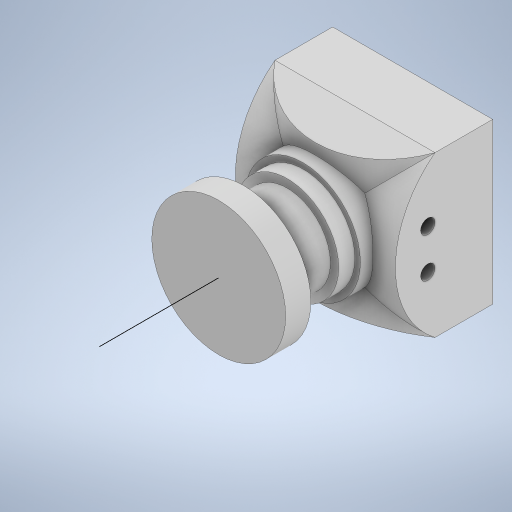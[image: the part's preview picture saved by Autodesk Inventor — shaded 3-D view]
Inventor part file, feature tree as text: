
AUTODESK INVENTOR PART (.ipt)
format: ipt  version: 2023 (Build 270158000, 158)  size: 365,568 bytes
history: native  units: in
note: dims shown in document units (in); Inventor stores cm internally (conversion verified against a paired STEP export)
features: sketch x12, extrude x9, projected_geometry x7, plane x2
ambient origin geometry x8: Origin, YZ Plane, XZ Plane, XY Plane, X Axis, Y Axis, Z Axis, Center Point
bodies: Solid1 (feature_tree)
feature tree (30):
  extrude  "Extrusion1"  Depth=0.874in
  extrude  "Extrusion2"  Depth=0.315in
  sketch  "Sketch3"  dims[d5=0.2854in d6=0.0in d9=0.2165in]
  extrude  "Extrusion4"  Depth=0.2165in
  extrude  "Extrusion5"  Depth=0.0886in
  extrude  "Extrusion6"  Depth=0.374in
  extrude  "Extrusion8"  Depth=0.0886in TaperAngle=0.0deg
  extrude  "Extrusion9"  Depth=0.2362in TaperAngle=0.0deg
  extrude  "Extrusion10"  Depth=0.1378in TaperAngle=0.0deg
  sketch  "Sketch12"  dims[d41=0.4409in]
  plane  "Work Plane2"
  extrude  "Extrusion12"  Depth=0.0394in
  plane  "Work Plane4"
  sketch  "Sketch18"  dims[d49=0.1083in d50=0.0787in d52=0.1083in d53=0.0787in d54=0.0in d55=0.0in d56=-0.437in]
  sketch  "Sketch1"  dims[d0=0.874in d1=0.874in]
  sketch  "Sketch2"  dims[d2=0.315in d3=0.0in d4=0.6299in]
  projected_geometry  "Projected Loop1"
  sketch  "Sketch5"  dims[d10=0.0886in d11=0.0in d12=0.2165in]
  projected_geometry  "Projected Loop3"
  sketch  "Sketch6"  dims[d13=0.0886in d14=0.0in d15=0.374in]
  projected_geometry  "Projected Loop4"
  sketch  "Sketch7"  dims[d16=0.0886in d17=0.0in d23=0.0886in d24=0.0in]
  projected_geometry  "Projected Loop5"
  sketch  "Sketch9"  dims[d25=0.0787in d26=0.2362in d27=0.0in]
  projected_geometry  "Projected Loop8"
  sketch  "Sketch10"  dims[d28=0.7307in d29=0.1378in d30=0.0in]
  projected_geometry  "Projected Loop9"
  sketch  "Sketch11"  dims[d31=1.063in d36=0.0394in]
  sketch  "Sketch17"  dims[d48=0.3543in]
  projected_geometry  "Projected Loop11"
